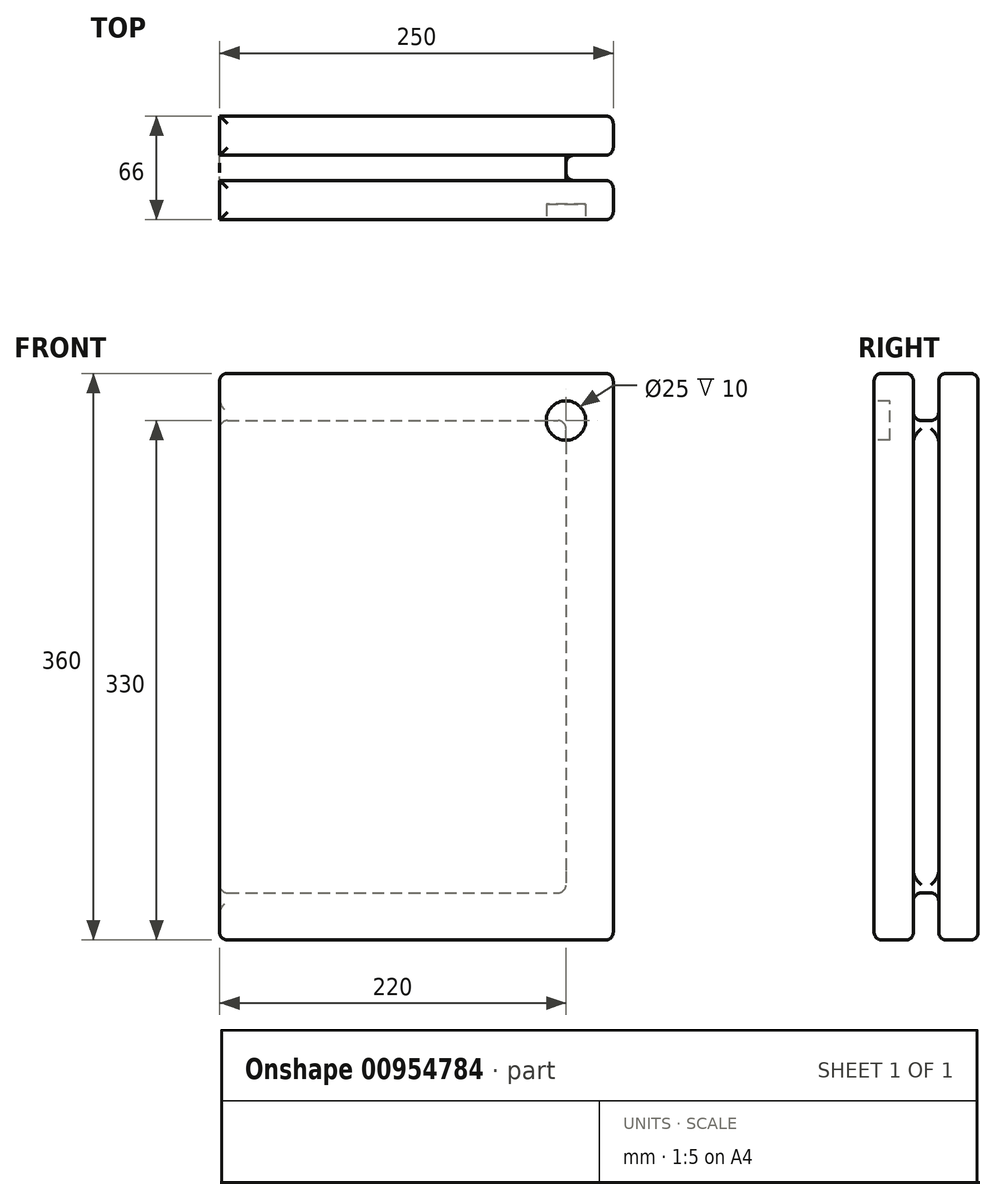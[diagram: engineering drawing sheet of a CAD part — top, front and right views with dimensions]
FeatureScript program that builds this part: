
annotation { "Feature Type Name" : "Feature", "Feature Type Description" : "" }
export const myFeature = defineFeature(function(context is Context, id is Id, definition is map)
    precondition{}
    {
        {
            var Q0;
            Q0=qCreatedBy(makeId("Right.planeOp"),FACE);
            var sketch = newSketch(context, id + "F0", { "sketchPlane" : qUnion([Q0])});
            skLineSegment(sketch, "E0", {"start": v(0, 0) * mm, "end": v(0, 150) * mm, "construction": true});
            skLineSegment(sketch, "E1", {"start": v(0, 0) * mm, "end": v(0, -150) * mm, "construction": true});
            skLineSegment(sketch, "E2", {"start": v(0, 150) * mm, "end": v(8, 150) * mm});
            skLineSegment(sketch, "E3", {"start": v(8, 150) * mm, "end": v(8, 180) * mm});
            skLineSegment(sketch, "E4", {"start": v(8, 180) * mm, "end": v(33, 180) * mm});
            skLineSegment(sketch, "E5", {"start": v(0, 0) * mm, "end": v(80, 0) * mm, "construction": true});
            skLineSegment(sketch, "E6", {"start": v(0, 0) * mm, "end": v(-80, 0) * mm, "construction": true});
            skLineSegment(sketch, "E7.MirrorCS", {"start": v(8, -180) * mm, "end": v(33, -180) * mm});
            skLineSegment(sketch, "E8.MirrorCS", {"start": v(8, -150) * mm, "end": v(8, -180) * mm});
            skLineSegment(sketch, "E9.MirrorCS", {"start": v(0, -150) * mm, "end": v(8, -150) * mm});
            skLineSegment(sketch, "E10", {"start": v(33, 180) * mm, "end": v(33, -180) * mm});
            skLineSegment(sketch, "E11", {"start": v(0, 150) * mm, "end": v(0, -150) * mm, "construction": true});
            skLineSegment(sketch, "E12.MirrorCS", {"start": v(0, 150) * mm, "end": v(-8, 150) * mm});
            skLineSegment(sketch, "E13.MirrorCS", {"start": v(-8, 150) * mm, "end": v(-8, 180) * mm});
            skLineSegment(sketch, "E14.MirrorCS", {"start": v(-8, 180) * mm, "end": v(-33, 180) * mm});
            skLineSegment(sketch, "E15.MirrorCS", {"start": v(-33, 180) * mm, "end": v(-33, -180) * mm});
            skLineSegment(sketch, "E16.MirrorCS", {"start": v(-8, -180) * mm, "end": v(-33, -180) * mm});
            skLineSegment(sketch, "E17.MirrorCS", {"start": v(-8, -150) * mm, "end": v(-8, -180) * mm});
            skLineSegment(sketch, "E18.MirrorCS", {"start": v(0, -150) * mm, "end": v(-8, -150) * mm});
            skSolve(sketch);
        }
        {
            var Q0;
            Q0=qCreatedBy(makeId("Front.planeOp"),FACE);
            var sketch = newSketch(context, id + "F1", { "sketchPlane" : qUnion([Q0])});
            skLineSegment(sketch, "E19", {"start": v(0, 0) * mm, "end": v(250, 0) * mm});
            skSolve(sketch);
        }
        {
            var Q0;
            Q0=qSketchRegion(id+"F0",true);
            var Q1;
            Q1=qConstructionFilter(qBodyType(qCreatedBy(id+"F1",EDGE),BodyType.WIRE),ConstructionObject.NO);
            sweep(context, id + "F2", {"profiles" : qUnion([Q0]), "path" : qUnion([Q1])});
        }
        {
            var Q0;
            Q0=makeQuery(id+"F2.opSweep","SWEPT_FACE",FACE,{"disambiguationData":[OSD([sQuery(id+"F0.wireOp",EDGE,"E15.MirrorCS"),sQuery(id+"F1.wireOp",EDGE,"E19")])]});
            var sketch = newSketch(context, id + "F3", { "sketchPlane" : qUnion([Q0])});
            skLineSegment(sketch, "E20", {"start": v(250, 180) * mm, "end": v(220, 180) * mm, "construction": true});
            skLineSegment(sketch, "E21", {"start": v(220, 180) * mm, "end": v(220, 150) * mm, "construction": true});
            skCircle(sketch, "E22", {"center": v(220, 150) * mm, "radius": 12.5 * mm});
            skSolve(sketch);
        }
        {
            var Q0;
            Q0=makeQuery(id+"F3.imprint","IMPRINT",FACE,{"disambiguationData":[TD([[makeQuery(id+"F3.imprint","IMPRINT",EDGE,{"derivedFrom":sQuery(id+"F3.wireOp",EDGE,"E22")}),1.0]])]});
            extrude(context, id + "F4", {"entities" : qUnion([Q0]), "operationType" : NewBodyOperationType.REMOVE, "oppositeDirection" : true, "depth" : 10 * mm, "offsetDistance" : 25 * mm});
        }
        {
            var Q0;
            Q0=makeQuery(id+"F2.opSweep","CAP_FACE",FACE,{"disambiguationData":[OSD([sQuery(id+"F0.wireOp",EDGE,"E2"),sQuery(id+"F0.wireOp",EDGE,"E3"),sQuery(id+"F0.wireOp",EDGE,"E4"),sQuery(id+"F0.wireOp",EDGE,"E7.MirrorCS"),sQuery(id+"F0.wireOp",EDGE,"E8.MirrorCS"),sQuery(id+"F0.wireOp",EDGE,"E9.MirrorCS"),sQuery(id+"F0.wireOp",EDGE,"E10"),sQuery(id+"F0.wireOp",EDGE,"E12.MirrorCS"),sQuery(id+"F0.wireOp",EDGE,"E13.MirrorCS"),sQuery(id+"F0.wireOp",EDGE,"E14.MirrorCS"),sQuery(id+"F0.wireOp",EDGE,"E15.MirrorCS"),sQuery(id+"F0.wireOp",EDGE,"E16.MirrorCS"),sQuery(id+"F0.wireOp",EDGE,"E17.MirrorCS"),sQuery(id+"F0.wireOp",EDGE,"E18.MirrorCS"),sQuery(id+"F1.wireOp",VERTEX,"E19.end")])],"isStart":false});
            var sketch = newSketch(context, id + "F5", { "sketchPlane" : qUnion([Q0])});
            skPoint(sketch, "E23", {"position": v(0, 0) * mm});
            skLineSegment(sketch, "E24", {"start": v(0, 0) * mm, "end": v(0, 150) * mm, "construction": true});
            skLineSegment(sketch, "E25", {"start": v(0, 0) * mm, "end": v(0, -150) * mm, "construction": true});
            skLineSegment(sketch, "E26", {"start": v(0, 150) * mm, "end": v(-8, 150) * mm});
            skLineSegment(sketch, "E27", {"start": v(-8, 150) * mm, "end": v(-8, -150) * mm});
            skLineSegment(sketch, "E28", {"start": v(-8, -150) * mm, "end": v(0, -150) * mm});
            skLineSegment(sketch, "E29.MirrorCS", {"start": v(0, 150) * mm, "end": v(8, 150) * mm});
            skLineSegment(sketch, "E30.MirrorCS", {"start": v(8, 150) * mm, "end": v(8, -150) * mm});
            skLineSegment(sketch, "E31.MirrorCS", {"start": v(8, -150) * mm, "end": v(0, -150) * mm});
            skSolve(sketch);
        }
        {
            var Q0;
            Q0=makeQuery(id+"F5.imprint","IMPRINT",FACE,{"disambiguationData":[TD([[makeQuery(id+"F5.imprint","IMPRINT",EDGE,{"derivedFrom":sQuery(id+"F5.wireOp",EDGE,"E26")}),1.0]])]});
            extrude(context, id + "F6", {"entities" : qUnion([Q0]), "operationType" : NewBodyOperationType.REMOVE, "oppositeDirection" : true, "depth" : 30 * mm, "offsetDistance" : 25 * mm});
        }
        {
            var Q0;
            Q0=makeQuery(id+"F2.opSweep","SWEPT_FACE",FACE,{"disambiguationData":[OSD([sQuery(id+"F0.wireOp",EDGE,"E2"),sQuery(id+"F0.wireOp",EDGE,"E12.MirrorCS"),sQuery(id+"F1.wireOp",EDGE,"E19")])]});
            var Q1;
            Q1=makeQuery(id+"F2.opSweep","SWEPT_FACE",FACE,{"disambiguationData":[OSD([sQuery(id+"F0.wireOp",EDGE,"E9.MirrorCS"),sQuery(id+"F0.wireOp",EDGE,"E18.MirrorCS"),sQuery(id+"F1.wireOp",EDGE,"E19")])]});
            var Q2;
            Q2=makeQuery(id+"F2.opSweep","SWEPT_FACE",FACE,{"disambiguationData":[OSD([sQuery(id+"F0.wireOp",EDGE,"E4"),sQuery(id+"F1.wireOp",EDGE,"E19")])]});
            var Q3;
            Q3=makeQuery(id+"F2.opSweep","SWEPT_FACE",FACE,{"disambiguationData":[OSD([sQuery(id+"F0.wireOp",EDGE,"E14.MirrorCS"),sQuery(id+"F1.wireOp",EDGE,"E19")])]});
            var Q4;
            {var subQ1=sQuery(id+"F0.wireOp",EDGE,"E8.MirrorCS");var subQ2=sQuery(id+"F0.wireOp",EDGE,"E7.MirrorCS");var subQ3=sQuery(id+"F0.wireOp",EDGE,"E4");var subQ4=sQuery(id+"F0.wireOp",EDGE,"E3");var subQ5=sQuery(id+"F0.wireOp",EDGE,"E10");Q4=makeQuery(id+"F6.boolean.opBoolean","SPLIT",FACE,{"disambiguationData":[TD([makeQuery(id+"F6.opExtrude","SWEPT_FACE",FACE,{"disambiguationData":[OSD([sQuery(id+"F5.wireOp",EDGE,"E30.MirrorCS")])]})])],"derivedFrom":makeQuery(id+"F2.opSweep","CAP_FACE",FACE,{"disambiguationData":[OSD([sQuery(id+"F0.wireOp",EDGE,"E2"),subQ4,subQ3,subQ2,subQ1,sQuery(id+"F0.wireOp",EDGE,"E9.MirrorCS"),subQ5,sQuery(id+"F0.wireOp",EDGE,"E12.MirrorCS"),sQuery(id+"F0.wireOp",EDGE,"E13.MirrorCS"),sQuery(id+"F0.wireOp",EDGE,"E14.MirrorCS"),sQuery(id+"F0.wireOp",EDGE,"E15.MirrorCS"),sQuery(id+"F0.wireOp",EDGE,"E16.MirrorCS"),sQuery(id+"F0.wireOp",EDGE,"E17.MirrorCS"),sQuery(id+"F0.wireOp",EDGE,"E18.MirrorCS"),sQuery(id+"F1.wireOp",VERTEX,"E19.end")])],"isStart":false})});}
            var Q5;
            {var subQ1=sQuery(id+"F0.wireOp",EDGE,"E16.MirrorCS");var subQ2=sQuery(id+"F0.wireOp",EDGE,"E15.MirrorCS");var subQ3=sQuery(id+"F0.wireOp",EDGE,"E14.MirrorCS");var subQ4=sQuery(id+"F0.wireOp",EDGE,"E13.MirrorCS");var subQ5=sQuery(id+"F0.wireOp",EDGE,"E17.MirrorCS");Q5=makeQuery(id+"F6.boolean.opBoolean","SPLIT",FACE,{"disambiguationData":[TD([makeQuery(id+"F6.opExtrude","SWEPT_FACE",FACE,{"disambiguationData":[OSD([sQuery(id+"F5.wireOp",EDGE,"E27")])]})])],"derivedFrom":makeQuery(id+"F2.opSweep","CAP_FACE",FACE,{"disambiguationData":[OSD([sQuery(id+"F0.wireOp",EDGE,"E2"),sQuery(id+"F0.wireOp",EDGE,"E3"),sQuery(id+"F0.wireOp",EDGE,"E4"),sQuery(id+"F0.wireOp",EDGE,"E7.MirrorCS"),sQuery(id+"F0.wireOp",EDGE,"E8.MirrorCS"),sQuery(id+"F0.wireOp",EDGE,"E9.MirrorCS"),sQuery(id+"F0.wireOp",EDGE,"E10"),sQuery(id+"F0.wireOp",EDGE,"E12.MirrorCS"),subQ4,subQ3,subQ2,subQ1,subQ5,sQuery(id+"F0.wireOp",EDGE,"E18.MirrorCS"),sQuery(id+"F1.wireOp",VERTEX,"E19.end")])],"isStart":false})});}
            var Q6;
            Q6=makeQuery(id+"F2.opSweep","SWEPT_FACE",FACE,{"disambiguationData":[OSD([sQuery(id+"F0.wireOp",EDGE,"E7.MirrorCS"),sQuery(id+"F1.wireOp",EDGE,"E19")])]});
            var Q7;
            Q7=makeQuery(id+"F2.opSweep","SWEPT_FACE",FACE,{"disambiguationData":[OSD([sQuery(id+"F0.wireOp",EDGE,"E16.MirrorCS"),sQuery(id+"F1.wireOp",EDGE,"E19")])]});
            fillet(context, id + "F7", {"entities" : qUnion([Q0, Q1, Q2, Q3, Q4, Q5, Q6, Q7]), "radius" : 5 * mm, "tangentPropagation" : true, "allowEdgeOverflow" : false});
        }
    });
